# Revit family: Bürocontainer
name_source: partatom
category: Grundstück
units: mm (PartAtom-declared; Revit-internal decimal feet)

## family parameters
Arbeitsebenenbasiert = Nein
Beim Laden mit Abzugskörper schneiden = Nein
Bemaßung runder Anschluss = Durchmesser verwenden
Gemeinsam genutzt = Nein
Immer vertikal = Ja
Teiletyp = Normal

## types (2) — shared parameters
Beschreibung = Baucontainer
Boden = Kunststoff - Laminat Hellbraun
Bodenstärke = 150 mm  [stored 0.492126 ft]
Breite = 2435 mm  [stored 7.98885 ft]
Breite Längsmodul = 1151 mm  [stored 3.77625 ft]
Breite Längsmodul doppelt = 2302 mm
Breite Quermodul = 1068 mm
Breite Quermodul doppelt = 2135 mm  [stored 7.00459 ft]
Containerrahmen = Autodesk Sky Blue 6-150-215
Containerwände = Metall - Trapezblech 210-215-220
Decke = Kunststoff - weiß 250-250-250
Deckelstärke = 150 mm  [stored 0.492126 ft]
Glas = Glas - Isolierverglasung Bronze
Länge = 6055 mm  [stored 19.8655 ft]
Rahmenfarbe Fenster & Türen = Autodesk Sky Blue 6-150-215
Sichtbeschläge = Metall - Edelstahl satiniert
Steherbreite = 150 mm  [stored 0.492126 ft]
Typenkommentare = Baucontainer
Türblatt = Autodesk Light Green 135-188-64
URL = www.autodesk.de/BIM
Wandfarbe innen = Kunststoff - weiß 250-250-250
Wandstärke = 100 mm  [stored 0.328084 ft]

## per-type parameters (varying)
| type | Höhe | Raumhöhe |
| H=2591 | 2591 mm | 2291 mm |
| H=2765 | 2765 mm  [stored 9.07152 ft] | 2465 mm  [stored 8.08727 ft] |

note: [stored X ft] marks values corroborated as IEEE doubles in the binary element streams (Revit-internal decimal feet)
